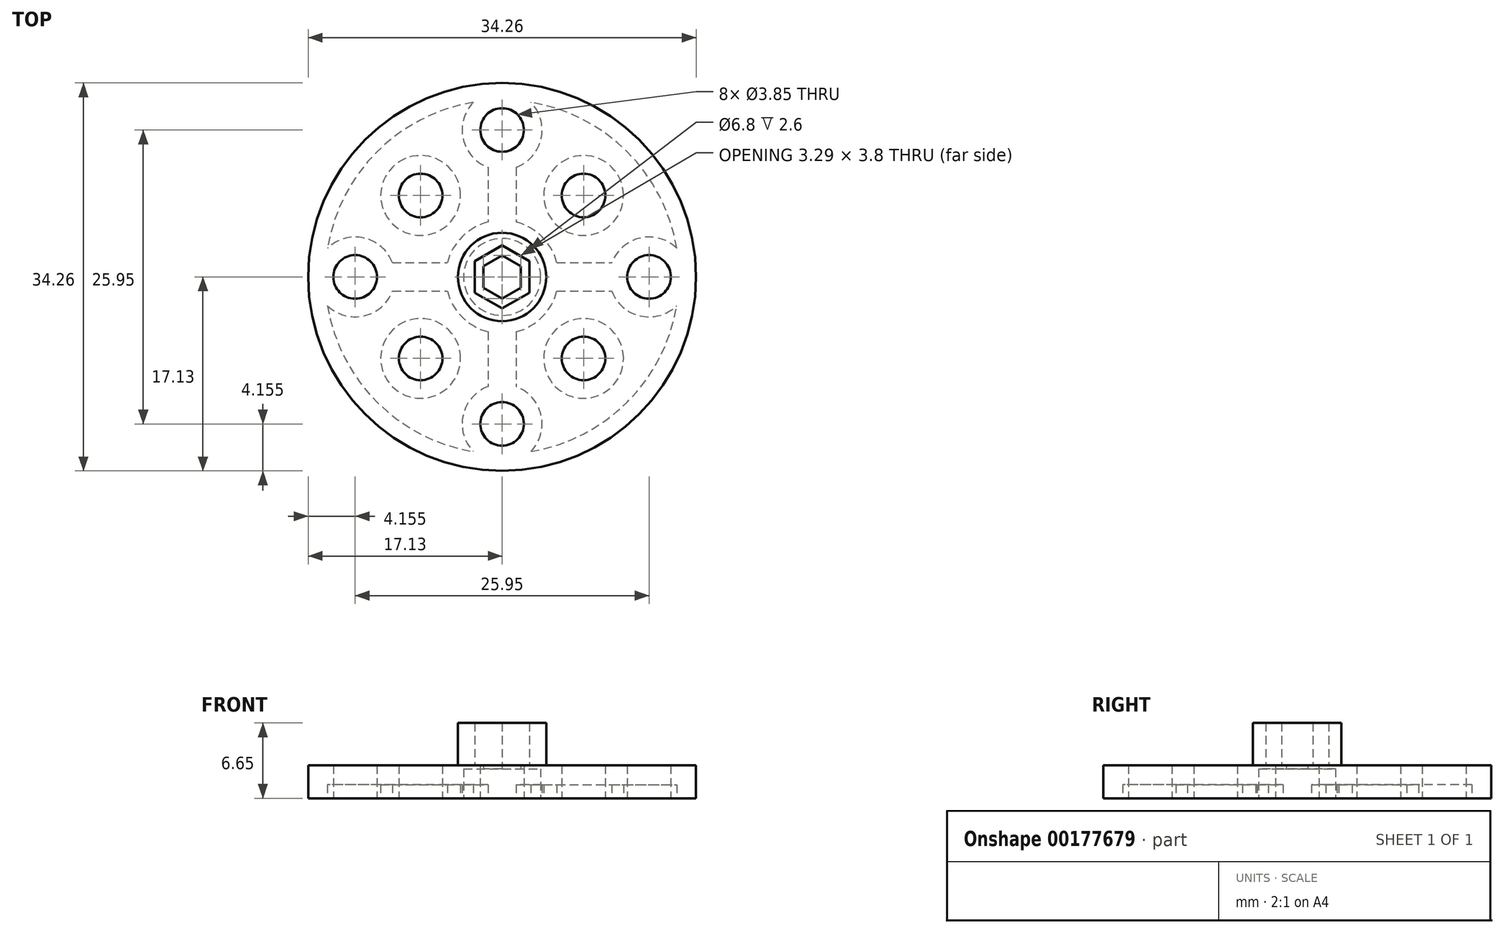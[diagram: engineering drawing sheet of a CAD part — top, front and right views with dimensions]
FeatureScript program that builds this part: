
annotation { "Feature Type Name" : "Feature", "Feature Type Description" : "" }
export const myFeature = defineFeature(function(context is Context, id is Id, definition is map)
    precondition{}
    {
        {
            var Q0;
            Q0=qCreatedBy(makeId("Top.planeOp"),FACE);
            var sketch = newSketch(context, id + "F0", { "sketchPlane" : qUnion([Q0])});
            skCircle(sketch, "E0", {"center": v(0, 0) * mm, "radius": 17.12 * mm});
            skCircle(sketch, "E1", {"center": v(0, 0) * mm, "radius": 3.9 * mm, "construction": true});
            skLineSegment(sketch, "E2", {"start": v(0, 17.12) * mm, "end": v(0, -17.12) * mm, "construction": true});
            skLineSegment(sketch, "E3", {"start": v(17.12, 0) * mm, "end": v(-17.12, 0) * mm, "construction": true});
            skCircle(sketch, "E4", {"center": v(12.97, 0) * mm, "radius": 1.93 * mm});
            skLineSegment(sketch, "E5", {"start": v(12.1, 12.1) * mm, "end": v(-12.1, -12.1) * mm, "construction": true});
            skLineSegment(sketch, "E6", {"start": v(0, -17.13) * mm, "end": v(-12.1, -12.1) * mm, "construction": true});
            skLineSegment(sketch, "E7", {"start": v(-17.13, 0) * mm, "end": v(-12.1, -12.1) * mm, "construction": true});
            skCircle(sketch, "E8", {"center": v(7.2, 7.2) * mm, "radius": 1.93 * mm});
            skCircle(sketch, "E9.1.0", {"center": v(-7.2, 7.2) * mm, "radius": 1.93 * mm});
            skCircle(sketch, "E9.2.0", {"center": v(-7.2, -7.2) * mm, "radius": 1.93 * mm});
            skCircle(sketch, "E9.3.0", {"center": v(7.2, -7.2) * mm, "radius": 1.93 * mm});
            skCircle(sketch, "E10.1.0", {"center": v(0, 12.97) * mm, "radius": 1.93 * mm});
            skCircle(sketch, "E10.2.0", {"center": v(-12.97, 0) * mm, "radius": 1.93 * mm});
            skCircle(sketch, "E10.3.0", {"center": v(0, -12.97) * mm, "radius": 1.93 * mm});
            skSolve(sketch);
        }
        {
            var Q0;
            Q0=makeQuery(id+"F0.imprint","IMPRINT",FACE,{"disambiguationData":[TD([[makeQuery(id+"F0.imprint","IMPRINT",EDGE,{"derivedFrom":sQuery(id+"F0.wireOp",EDGE,"E0")}),1.0]])]});
            extrude(context, id + "F1", {"entities" : qUnion([Q0]), "depth" : 2.9 * mm});
        }
        {
            var Q0;
            Q0=makeQuery(id+"F1.opExtrude","CAP_FACE",FACE,{"disambiguationData":[OSD([sQuery(id+"F0.wireOp",EDGE,"E0"),sQuery(id+"F0.wireOp",EDGE,"E4"),sQuery(id+"F0.wireOp",EDGE,"E8"),sQuery(id+"F0.wireOp",EDGE,"E9.1.0"),sQuery(id+"F0.wireOp",EDGE,"E9.2.0"),sQuery(id+"F0.wireOp",EDGE,"E9.3.0"),sQuery(id+"F0.wireOp",EDGE,"E10.1.0"),sQuery(id+"F0.wireOp",EDGE,"E10.2.0"),sQuery(id+"F0.wireOp",EDGE,"E10.3.0")])],"isStart":false});
            var sketch = newSketch(context, id + "F2", { "sketchPlane" : qUnion([Q0])});
            skCircle(sketch, "E11", {"center": v(0, 0) * mm, "radius": 3.9 * mm});
            skCircle(sketch, "E12.cCircle", {"center": v(0, 0) * mm, "radius": 2.4 * mm, "construction": true});
            skLineSegment(sketch, "E12.0", {"start": v(2.4, 1.39) * mm, "end": v(2.4, -1.39) * mm});
            skLineSegment(sketch, "E12.1", {"start": v(2.4, -1.39) * mm, "end": v(0, -2.78) * mm});
            skLineSegment(sketch, "E12.2", {"start": v(0, -2.77) * mm, "end": v(-2.4, -1.39) * mm});
            skLineSegment(sketch, "E12.3", {"start": v(-2.4, -1.39) * mm, "end": v(-2.4, 1.39) * mm});
            skLineSegment(sketch, "E12.4", {"start": v(-2.4, 1.39) * mm, "end": v(0, 2.78) * mm});
            skLineSegment(sketch, "E12.5", {"start": v(0, 2.78) * mm, "end": v(2.4, 1.39) * mm});
            skPoint(sketch, "E12.0.midPoint", {"position": v(2.4, 0) * mm});
            skSolve(sketch);
        }
        {
            var Q0;
            Q0=makeQuery(id+"F2.imprint","IMPRINT",FACE,{"disambiguationData":[TD([[makeQuery(id+"F2.imprint","IMPRINT",EDGE,{"derivedFrom":sQuery(id+"F2.wireOp",EDGE,"E11")}),1.0]])]});
            extrude(context, id + "F3", {"entities" : qUnion([Q0]), "operationType" : NewBodyOperationType.ADD, "depth" : 3.75 * mm});
        }
        {
            var Q0;
            Q0=makeQuery(id+"F1.opExtrude","CAP_FACE",FACE,{"disambiguationData":[OSD([sQuery(id+"F0.wireOp",EDGE,"E0"),sQuery(id+"F0.wireOp",EDGE,"E4"),sQuery(id+"F0.wireOp",EDGE,"E8"),sQuery(id+"F0.wireOp",EDGE,"E9.1.0"),sQuery(id+"F0.wireOp",EDGE,"E9.2.0"),sQuery(id+"F0.wireOp",EDGE,"E9.3.0"),sQuery(id+"F0.wireOp",EDGE,"E10.1.0"),sQuery(id+"F0.wireOp",EDGE,"E10.2.0"),sQuery(id+"F0.wireOp",EDGE,"E10.3.0")])],"isStart":true});
            var sketch = newSketch(context, id + "F4", { "sketchPlane" : qUnion([Q0])});
            skCircle(sketch, "E13", {"center": v(0, 0) * mm, "radius": 15.62 * mm});
            skPoint(sketch, "E14", {"position": v(-12.97, 0) * mm});
            skPoint(sketch, "E15", {"position": v(-7.2, -7.2) * mm});
            skPoint(sketch, "E16", {"position": v(0, -12.97) * mm});
            skPoint(sketch, "E17", {"position": v(7.2, -7.2) * mm});
            skPoint(sketch, "E18", {"position": v(12.97, 0) * mm});
            skPoint(sketch, "E19", {"position": v(7.2, 7.2) * mm});
            skPoint(sketch, "E20", {"position": v(0, 12.97) * mm});
            skPoint(sketch, "E21", {"position": v(-7.2, 7.2) * mm});
            skCircle(sketch, "E22", {"center": v(0, 0) * mm, "radius": 3.4 * mm});
            skCircle(sketch, "E23", {"center": v(-7.2, -7.2) * mm, "radius": 3.53 * mm});
            skCircle(sketch, "E24", {"center": v(0, -12.97) * mm, "radius": 3.53 * mm});
            skCircle(sketch, "E25.1.0", {"center": v(7.2, -7.2) * mm, "radius": 3.53 * mm});
            skCircle(sketch, "E25.2.0", {"center": v(7.2, 7.2) * mm, "radius": 3.53 * mm});
            skCircle(sketch, "E25.3.0", {"center": v(-7.2, 7.2) * mm, "radius": 3.53 * mm});
            skCircle(sketch, "E26.1.0", {"center": v(12.97, 0) * mm, "radius": 3.53 * mm});
            skCircle(sketch, "E26.2.0", {"center": v(0, 12.97) * mm, "radius": 3.53 * mm});
            skCircle(sketch, "E26.3.0", {"center": v(-12.97, 0) * mm, "radius": 3.53 * mm});
            skCircle(sketch, "E27", {"center": v(0, 0) * mm, "radius": 5 * mm});
            skLineSegment(sketch, "E28", {"start": v(5, 0) * mm, "end": v(9.45, 0) * mm});
            skLineSegment(sketch, "E29", {"start": v(4.84, -1.25) * mm, "end": v(9.68, -1.25) * mm});
            skLineSegment(sketch, "E30", {"start": v(4.84, 1.25) * mm, "end": v(9.68, 1.25) * mm});
            skLineSegment(sketch, "E31", {"start": v(-5, 0) * mm, "end": v(-9.45, 0) * mm});
            skLineSegment(sketch, "E32", {"start": v(-9.68, -1.25) * mm, "end": v(-4.84, -1.25) * mm});
            skLineSegment(sketch, "E33", {"start": v(-9.68, 1.25) * mm, "end": v(-4.84, 1.25) * mm});
            skLineSegment(sketch, "E34", {"start": v(0, -5) * mm, "end": v(0, -9.45) * mm});
            skLineSegment(sketch, "E35", {"start": v(-1.25, -9.68) * mm, "end": v(-1.25, -4.84) * mm});
            skLineSegment(sketch, "E36", {"start": v(1.25, -9.68) * mm, "end": v(1.25, -4.84) * mm});
            skLineSegment(sketch, "E37", {"start": v(0, 5) * mm, "end": v(0, 9.45) * mm});
            skLineSegment(sketch, "E38", {"start": v(-1.25, 4.84) * mm, "end": v(-1.25, 9.68) * mm});
            skLineSegment(sketch, "E39", {"start": v(1.25, 4.84) * mm, "end": v(1.25, 9.68) * mm});
            skCircle(sketch, "E40.cCircle", {"center": v(0, 0) * mm, "radius": 1.65 * mm, "construction": true});
            skLineSegment(sketch, "E40.0", {"start": v(1.65, 0.95) * mm, "end": v(1.65, -0.95) * mm});
            skLineSegment(sketch, "E40.1", {"start": v(1.65, -0.95) * mm, "end": v(0, -1.9) * mm});
            skLineSegment(sketch, "E40.2", {"start": v(0, -1.9) * mm, "end": v(-1.65, -0.95) * mm});
            skLineSegment(sketch, "E40.3", {"start": v(-1.65, -0.95) * mm, "end": v(-1.65, 0.95) * mm});
            skLineSegment(sketch, "E40.4", {"start": v(-1.65, 0.95) * mm, "end": v(0, 1.9) * mm});
            skLineSegment(sketch, "E40.5", {"start": v(0, 1.9) * mm, "end": v(1.65, 0.95) * mm});
            skPoint(sketch, "E40.0.midPoint", {"position": v(1.65, 0) * mm});
            skSolve(sketch);
        }
        {
            var Q0;
            Q0=makeQuery(id+"F4.imprint","IMPRINT",FACE,{"disambiguationData":[TD([[makeQuery(id+"F4.imprint","IMPRINT",EDGE,{"derivedFrom":sQuery(id+"F4.wireOp",EDGE,"E25.1.0")}),-1.0]])]});
            var Q1;
            Q1=makeQuery(id+"F4.imprint","IMPRINT",FACE,{"disambiguationData":[TD([[makeQuery(id+"F4.imprint","IMPRINT",EDGE,{"derivedFrom":sQuery(id+"F4.wireOp",EDGE,"E25.2.0")}),-1.0]])]});
            var Q2;
            Q2=makeQuery(id+"F4.imprint","IMPRINT",FACE,{"disambiguationData":[TD([[makeQuery(id+"F4.imprint","IMPRINT",EDGE,{"derivedFrom":sQuery(id+"F4.wireOp",EDGE,"E25.3.0")}),-1.0]])]});
            var Q3;
            Q3=makeQuery(id+"F4.imprint","IMPRINT",FACE,{"disambiguationData":[TD([[makeQuery(id+"F4.imprint","IMPRINT",EDGE,{"derivedFrom":sQuery(id+"F4.wireOp",EDGE,"E23")}),-1.0]])]});
            extrude(context, id + "F5", {"entities" : qUnion([Q0, Q1, Q2, Q3]), "operationType" : NewBodyOperationType.REMOVE, "oppositeDirection" : true, "depth" : 1.2 * mm});
        }
        {
            var Q0;
            Q0=makeQuery(id+"F4.imprint","IMPRINT",FACE,{"disambiguationData":[TD([[makeQuery(id+"F4.imprint","IMPRINT",EDGE,{"derivedFrom":sQuery(id+"F4.wireOp",EDGE,"E22")}),1.0]])]});
            extrude(context, id + "F6", {"entities" : qUnion([Q0]), "operationType" : NewBodyOperationType.REMOVE, "oppositeDirection" : true, "depth" : 2.6 * mm});
        }
        {
            var Q0;
            Q0=makeQuery(id+"F4.imprint","IMPRINT",FACE,{"disambiguationData":[TD([[makeQuery(id+"F4.imprint","IMPRINT",EDGE,{"derivedFrom":sQuery(id+"F4.wireOp",EDGE,"E40.0")}),-1.0]])]});
            extrude(context, id + "F7", {"entities" : qUnion([Q0]), "operationType" : NewBodyOperationType.REMOVE, "oppositeDirection" : true, "depth" : 25 * mm});
        }
    });
